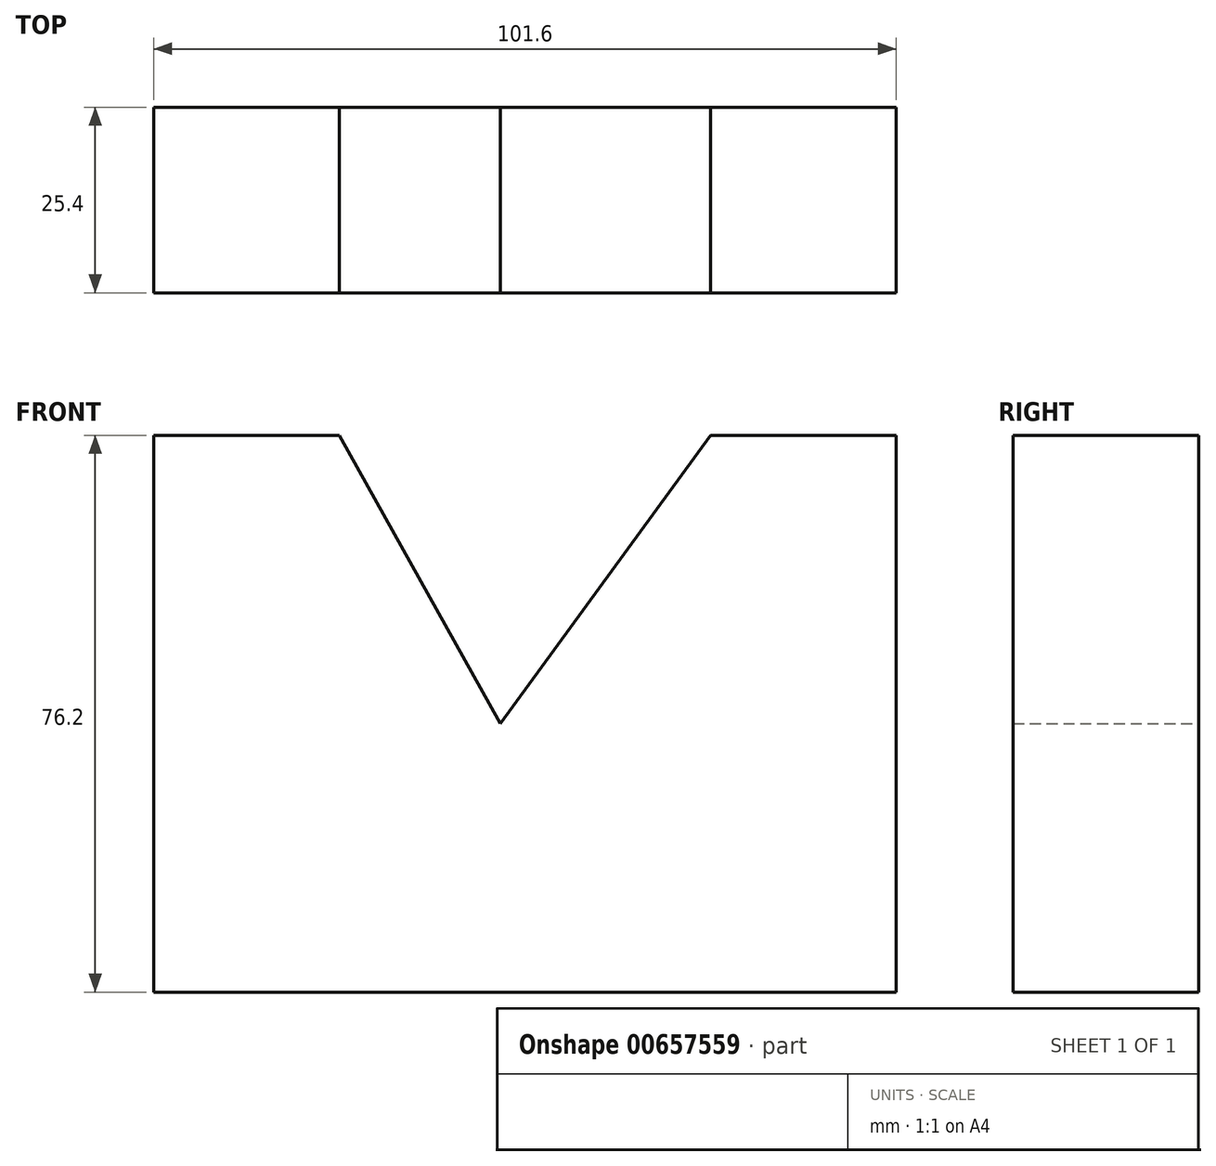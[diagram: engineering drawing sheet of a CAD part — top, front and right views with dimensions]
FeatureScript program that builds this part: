
annotation { "Feature Type Name" : "Feature", "Feature Type Description" : "" }
export const myFeature = defineFeature(function(context is Context, id is Id, definition is map)
    precondition{}
    {
        {
            var Q0;
            Q0=qCreatedBy(makeId("Front.planeOp"),FACE);
            var sketch = newSketch(context, id + "F0", { "sketchPlane" : qUnion([Q0])});
            skLineSegment(sketch, "E0", {"start": v(-40.78, -36.75) * mm, "end": v(60.82, -36.75) * mm});
            skLineSegment(sketch, "E1", {"start": v(60.82, -36.75) * mm, "end": v(60.82, 39.45) * mm});
            skLineSegment(sketch, "E2", {"start": v(60.82, 39.45) * mm, "end": v(35.42, 39.45) * mm});
            skLineSegment(sketch, "E3", {"start": v(-40.78, -36.75) * mm, "end": v(-40.78, 39.45) * mm});
            skLineSegment(sketch, "E4", {"start": v(-40.78, 39.45) * mm, "end": v(-15.38, 39.45) * mm});
            skLineSegment(sketch, "E5", {"start": v(-15.38, 39.45) * mm, "end": v(6.67, 0) * mm});
            skLineSegment(sketch, "E6", {"start": v(35.42, 39.45) * mm, "end": v(6.67, 0) * mm});
            skSolve(sketch);
        }
        {
            var Q0;
            Q0=makeQuery(id+"F0.imprint","IMPRINT",FACE,{"disambiguationData":[TD([[makeQuery(id+"F0.imprint","IMPRINT",EDGE,{"derivedFrom":sQuery(id+"F0.wireOp",EDGE,"E0")}),1.0]])]});
            extrude(context, id + "F1", {"entities" : qUnion([Q0]), "depth" : 25.4 * mm, "offsetDistance" : 25.4 * mm});
        }
    });
